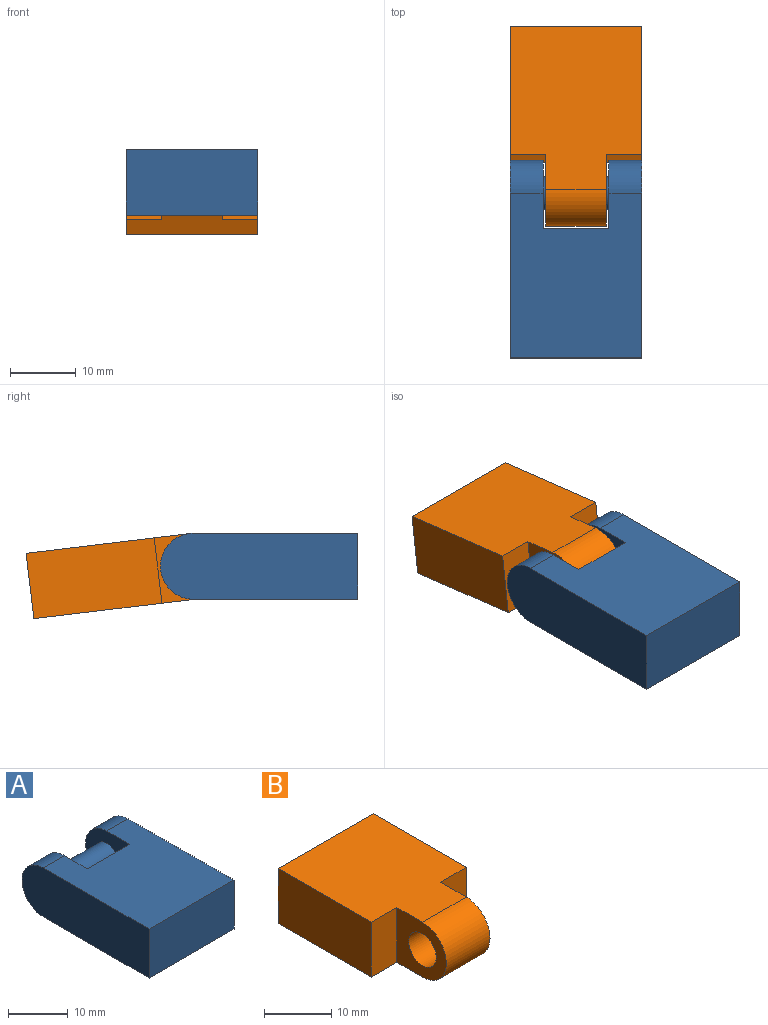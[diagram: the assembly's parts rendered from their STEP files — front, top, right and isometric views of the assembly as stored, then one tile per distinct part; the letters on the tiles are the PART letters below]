
ASSEMBLY  parts=2 mates=1
PART A: 11 faces, bbox 20x30x10 mm
  f0: plane 25x20mm, normal (0,0,-1), area 446mm2, adj f1,f3,f4,f5,f6,f7,f8,f9
  f1: cylinder r=5mm len=10mm, axis (-1,0,0), area 78.5mm2, adj f0,f2,f6,f7
  f2: plane 25x20mm, normal (0,0,1), area 446mm2, adj f1,f3,f4,f5,f6,f7,f8,f9
  f3: cylinder r=5mm len=10mm, axis (-1,0,0), area 78.5mm2, adj f0,f2,f5,f9
  f4: plane 20x10mm, normal (0,-1,0), area 200mm2, adj f0,f2,f5,f6
  f5: plane 30x10mm, normal (1,0,0), area 289.3mm2, adj f0,f2,f3,f4
  f6: plane 30x10mm, normal (-1,0,0), area 289.3mm2, adj f0,f1,f2,f4
  f7: plane 10.4x10mm, normal (1,0,0), area 73.6mm2, adj f0,f1,f2,f8,f10
  f8: plane 10x10mm, normal (0,1,0), area 100mm2, adj f0,f2,f7,f9
  f9: plane 10.4x10mm, normal (-1,0,0), area 73.6mm2, adj f0,f2,f3,f8,f10
  f10: cylinder r=2.5mm len=10mm, axis (-1,0,0), area 157.1mm2, adj f7,f9
PART B: 11 faces, bbox 20x30x10 mm
  f0: plane 10x5.4mm, normal (0,-1,0), area 54mm2, adj f2,f4,f6,f10
  f1: plane 10x5.4mm, normal (0,-1,0), area 54mm2, adj f2,f4,f5,f9
  f2: plane 25x20mm, normal (0,0,-1), area 441.7mm2, adj f0,f1,f3,f5,f6,f7,f9,f10
  f3: plane 20x10mm, normal (0,1,0), area 200mm2, adj f2,f4,f5,f6
  f4: plane 25x20mm, normal (0,0,1), area 441.7mm2, adj f0,f1,f3,f5,f6,f7,f9,f10
  f5: plane 19.6x10mm, normal (1,0,0), area 196mm2, adj f1,f2,f3,f4
  f6: plane 19.6x10mm, normal (-1,0,0), area 196mm2, adj f0,f2,f3,f4
  f7: cylinder r=5mm len=10mm, axis (-1,0,0), area 144.5mm2, adj f2,f4,f9,f10
  f8: cylinder r=2.9mm len=9.2mm, axis (-1,0,0), area 167.6mm2, adj f9,f10
  f9: plane 10.4x10mm, normal (1,0,0), area 66.8mm2, adj f1,f2,f4,f7,f8
  f10: plane 10.4x10mm, normal (-1,0,0), area 66.8mm2, adj f0,f2,f4,f7,f8
PLACE A t=(-2.3,-1.59,13.94)mm fixed
PLACE B rot(axis=(-1,0,0),6.9deg) t=(-2.3,-1.59,13.94)mm
MATE revolute A.f10 <-> B.f7  axis (-1,0,0) through (-2.3,-1.59,13.94)mm
